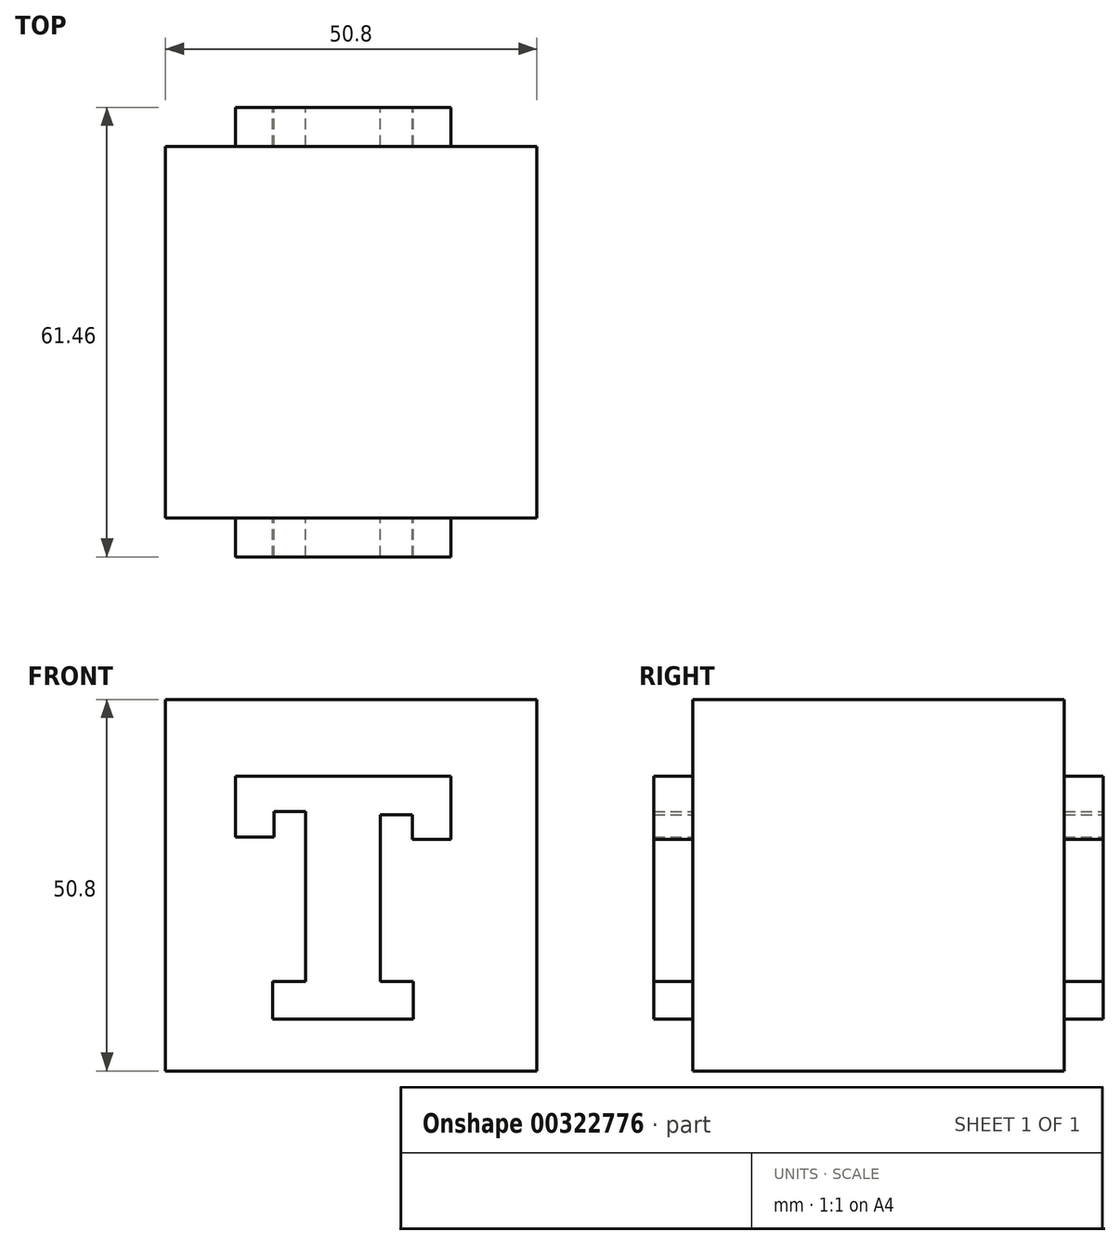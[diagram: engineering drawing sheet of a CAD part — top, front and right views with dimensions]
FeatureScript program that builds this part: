
annotation { "Feature Type Name" : "Feature", "Feature Type Description" : "" }
export const myFeature = defineFeature(function(context is Context, id is Id, definition is map)
    precondition{}
    {
        {
            var Q0;
            Q0=qCreatedBy(makeId("Front.planeOp"),FACE);
            var sketch = newSketch(context, id + "F0", { "sketchPlane" : qUnion([Q0])});
            skLineSegment(sketch, "E0.bottom", {"start": v(-24.05, 30.56) * mm, "end": v(26.75, 30.56) * mm});
            skLineSegment(sketch, "E0.top", {"start": v(-24.05, -20.24) * mm, "end": v(26.75, -20.24) * mm});
            skLineSegment(sketch, "E0.left", {"start": v(-24.05, 30.56) * mm, "end": v(-24.05, -20.24) * mm});
            skLineSegment(sketch, "E0.right", {"start": v(26.75, 30.56) * mm, "end": v(26.75, -20.24) * mm});
            skSolve(sketch);
        }
        {
            var Q0;
            Q0=makeQuery(id+"F0.imprint","IMPRINT",FACE,{"disambiguationData":[TD([[makeQuery(id+"F0.imprint","IMPRINT",EDGE,{"derivedFrom":sQuery(id+"F0.wireOp",EDGE,"E0.bottom")}),-1.0]])]});
            extrude(context, id + "F1", {"entities" : qUnion([Q0]), "endBound" : BoundingType.SYMMETRIC, "depth" : 50.8 * mm});
        }
        {
            var Q0;
            Q0=qCreatedBy(makeId("Front.planeOp"),FACE);
            var sketch = newSketch(context, id + "F2", { "sketchPlane" : qUnion([Q0])});
            skLineSegment(sketch, "E1", {"start": v(-9.41, -13.17) * mm, "end": v(9.84, -13.17) * mm});
            skLineSegment(sketch, "E2", {"start": v(-9.41, -13.17) * mm, "end": v(-9.41, -8.03) * mm});
            skLineSegment(sketch, "E3", {"start": v(9.84, -13.17) * mm, "end": v(9.84, -8.03) * mm});
            skLineSegment(sketch, "E4", {"start": v(9.84, -8.03) * mm, "end": v(5.33, -8.03) * mm});
            skLineSegment(sketch, "E5", {"start": v(-9.41, -8.03) * mm, "end": v(-4.89, -8.03) * mm});
            skLineSegment(sketch, "E6", {"start": v(-4.89, -8.03) * mm, "end": v(-4.89, 15.22) * mm});
            skLineSegment(sketch, "E7", {"start": v(5.33, -8.03) * mm, "end": v(5.33, 14.78) * mm});
            skLineSegment(sketch, "E8", {"start": v(5.33, 14.78) * mm, "end": v(9.73, 14.78) * mm});
            skLineSegment(sketch, "E9", {"start": v(-4.89, 15.22) * mm, "end": v(-9.2, 15.22) * mm});
            skLineSegment(sketch, "E10", {"start": v(-9.2, 15.22) * mm, "end": v(-9.2, 11.76) * mm});
            skLineSegment(sketch, "E11", {"start": v(9.73, 14.78) * mm, "end": v(9.73, 11.45) * mm});
            skLineSegment(sketch, "E12", {"start": v(9.73, 11.45) * mm, "end": v(15, 11.45) * mm});
            skLineSegment(sketch, "E13", {"start": v(-9.2, 11.76) * mm, "end": v(-14.47, 11.76) * mm});
            skLineSegment(sketch, "E14", {"start": v(-14.47, 11.76) * mm, "end": v(-14.47, 20.04) * mm});
            skLineSegment(sketch, "E15", {"start": v(15, 11.45) * mm, "end": v(15, 20.04) * mm});
            skLineSegment(sketch, "E16", {"start": v(15, 20.04) * mm, "end": v(-14.47, 20.04) * mm});
            skPoint(sketch, "E17.endSnap0", {"position": v(-11.84, 11.76) * mm});
            skSolve(sketch);
        }
        {
            var Q0;
            Q0 = qSketchRegion(id + "F2", true);
            extrude(context, id + "F3", {"entities" : qUnion([Q0]), "operationType" : NewBodyOperationType.ADD, "depth" : 30.73 * mm, "hasSecondDirection" : true, "secondDirectionOppositeDirection" : true, "secondDirectionDepth" : 30.73 * mm});
        }
    });
